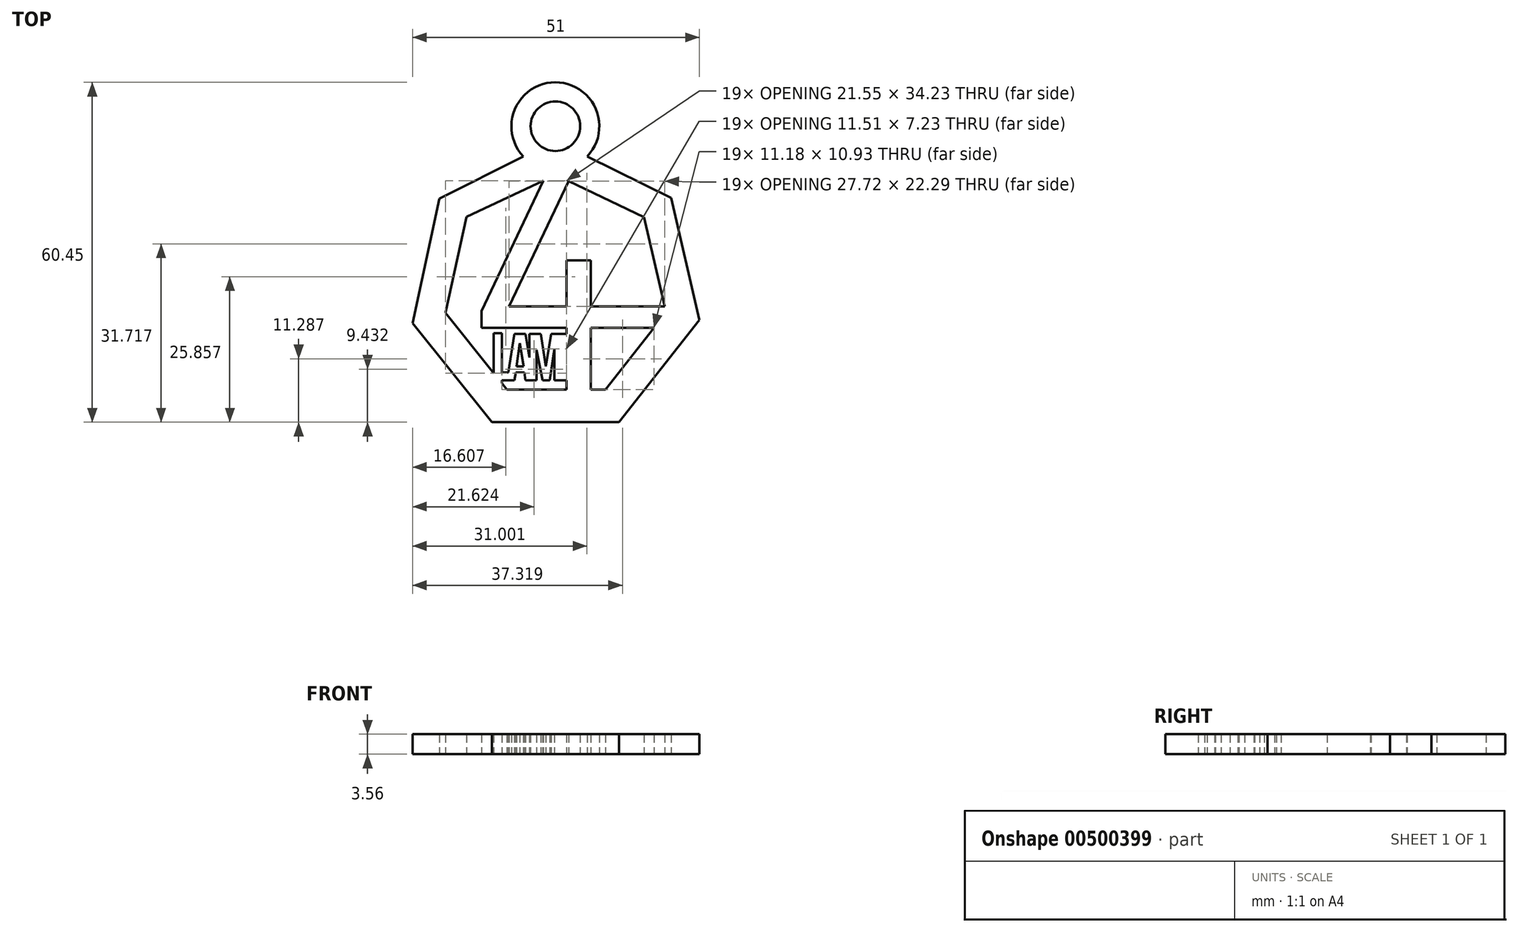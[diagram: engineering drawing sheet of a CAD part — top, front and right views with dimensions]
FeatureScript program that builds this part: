
annotation { "Feature Type Name" : "Feature", "Feature Type Description" : "" }
export const myFeature = defineFeature(function(context is Context, id is Id, definition is map)
    precondition{}
    {
        {
            var Q0;
            Q0=qCreatedBy(makeId("Top.planeOp"),FACE);
            var sketch = newSketch(context, id + "F0", { "sketchPlane" : qUnion([Q0])});
            skPoint(sketch, "E0.middle", {"position": v(0, 0) * mm});
            skLineSegment(sketch, "E1", {"start": v(5.7, 22.4) * mm, "end": v(20.58, 15.04) * mm});
            skLineSegment(sketch, "E2", {"start": v(20.58, 15.04) * mm, "end": v(25.61, -6.7) * mm});
            skLineSegment(sketch, "E3", {"start": v(25.61, -6.7) * mm, "end": v(11.33, -24.87) * mm});
            skLineSegment(sketch, "E4", {"start": v(11.33, -24.87) * mm, "end": v(-11.3, -24.87) * mm});
            skLineSegment(sketch, "E5", {"start": v(-11.3, -24.87) * mm, "end": v(-25.4, -7.27) * mm});
            skLineSegment(sketch, "E6", {"start": v(-25.4, -7.27) * mm, "end": v(-20.6, 14.93) * mm});
            skLineSegment(sketch, "E7", {"start": v(-20.6, 14.93) * mm, "end": v(-5.68, 22.4) * mm});
            skLineSegment(sketch, "E8", {"start": v(-15.79, 11.68) * mm, "end": v(-2.17, 18.1) * mm});
            skLineSegment(sketch, "E9", {"start": v(2.37, 18) * mm, "end": v(15.8, 11.6) * mm});
            skLineSegment(sketch, "E10", {"start": v(15.8, 11.6) * mm, "end": v(19.47, -4.3) * mm});
            skLineSegment(sketch, "E11", {"start": v(17.52, -8.12) * mm, "end": v(8.92, -19.05) * mm});
            skLineSegment(sketch, "E12", {"start": v(8.92, -19.05) * mm, "end": v(6.34, -19.05) * mm});
            skLineSegment(sketch, "E13", {"start": v(-8.61, -19.05) * mm, "end": v(-9.52, -17.92) * mm});
            skLineSegment(sketch, "E14", {"start": v(-19.56, -5.45) * mm, "end": v(-15.79, 11.68) * mm});
            skLineSegment(sketch, "E15", {"start": v(2.37, 18) * mm, "end": v(-8.25, -4.3) * mm});
            skLineSegment(sketch, "E16", {"start": v(-8.25, -4.3) * mm, "end": v(1.99, -4.3) * mm});
            skLineSegment(sketch, "E17", {"start": v(1.99, -4.3) * mm, "end": v(1.99, 3.9) * mm});
            skLineSegment(sketch, "E18", {"start": v(1.99, 3.9) * mm, "end": v(6.34, 3.9) * mm});
            skLineSegment(sketch, "E19", {"start": v(6.34, 3.9) * mm, "end": v(6.34, -4.3) * mm});
            skLineSegment(sketch, "E20", {"start": v(6.34, -4.3) * mm, "end": v(19.47, -4.3) * mm});
            skLineSegment(sketch, "E21", {"start": v(17.52, -8.12) * mm, "end": v(6.34, -8.12) * mm});
            skLineSegment(sketch, "E22", {"start": v(6.34, -8.12) * mm, "end": v(6.34, -19.05) * mm});
            skLineSegment(sketch, "E23", {"start": v(1.99, -19.05) * mm, "end": v(1.99, -17.43) * mm});
            skLineSegment(sketch, "E24", {"start": v(1.99, -8.12) * mm, "end": v(-13.1, -8.12) * mm});
            skLineSegment(sketch, "E25", {"start": v(-13.1, -8.12) * mm, "end": v(-13.1, -5.12) * mm});
            skLineSegment(sketch, "E26", {"start": v(-13.1, -5.12) * mm, "end": v(-2.17, 18.1) * mm});
            skLineSegment(sketch, "E27", {"start": v(-10.97, -16.13) * mm, "end": v(-10.97, -9.02) * mm});
            skLineSegment(sketch, "E28", {"start": v(-10.97, -9.02) * mm, "end": v(-9.52, -9.02) * mm});
            skLineSegment(sketch, "E29", {"start": v(-9.52, -9.02) * mm, "end": v(-9.52, -16) * mm});
            skLineSegment(sketch, "E30", {"start": v(-7.28, -9.15) * mm, "end": v(-5.28, -9.15) * mm});
            skLineSegment(sketch, "E31", {"start": v(-5.28, -9.15) * mm, "end": v(-4.6, -13.39) * mm});
            skLineSegment(sketch, "E32", {"start": v(-4.6, -13.39) * mm, "end": v(-4.6, -9.15) * mm});
            skLineSegment(sketch, "E33", {"start": v(-4.6, -9.15) * mm, "end": v(-2.6, -9.15) * mm});
            skLineSegment(sketch, "E34", {"start": v(-2.6, -9.15) * mm, "end": v(-1.67, -14.94) * mm});
            skLineSegment(sketch, "E35", {"start": v(-1.67, -14.94) * mm, "end": v(-0.73, -9.15) * mm});
            skLineSegment(sketch, "E36", {"start": v(-0.73, -9.15) * mm, "end": v(1.99, -9.15) * mm});
            skLineSegment(sketch, "E37", {"start": v(-7.28, -9.15) * mm, "end": v(-8.38, -16) * mm});
            skLineSegment(sketch, "E38", {"start": v(-8.61, -17.43) * mm, "end": v(-7.28, -17.43) * mm});
            skLineSegment(sketch, "E39", {"start": v(-7.28, -17.43) * mm, "end": v(-7.05, -16) * mm});
            skLineSegment(sketch, "E40", {"start": v(-7.05, -16) * mm, "end": v(-5.53, -16) * mm});
            skLineSegment(sketch, "E41", {"start": v(-5.53, -16) * mm, "end": v(-5.3, -17.43) * mm});
            skLineSegment(sketch, "E42", {"start": v(-5.3, -17.43) * mm, "end": v(-3.35, -17.43) * mm});
            skLineSegment(sketch, "E43", {"start": v(-3.35, -17.43) * mm, "end": v(-3.35, -12.02) * mm});
            skLineSegment(sketch, "E44", {"start": v(-3.35, -12.02) * mm, "end": v(-2.27, -17.43) * mm});
            skLineSegment(sketch, "E45", {"start": v(-2.27, -17.43) * mm, "end": v(-1, -17.43) * mm});
            skLineSegment(sketch, "E46", {"start": v(-1, -17.43) * mm, "end": v(-0.2, -11.82) * mm});
            skLineSegment(sketch, "E47", {"start": v(-0.2, -11.82) * mm, "end": v(-0.2, -17.43) * mm});
            skLineSegment(sketch, "E48", {"start": v(-0.2, -17.43) * mm, "end": v(1.99, -17.43) * mm});
            skLineSegment(sketch, "E49", {"start": v(-6.32, -10.81) * mm, "end": v(-6.9, -14.94) * mm});
            skLineSegment(sketch, "E50", {"start": v(-6.9, -14.94) * mm, "end": v(-5.6, -14.94) * mm});
            skLineSegment(sketch, "E51", {"start": v(-5.6, -14.94) * mm, "end": v(-6.32, -10.81) * mm});
            skLineSegment(sketch, "E52.trimOffspring", {"start": v(1.99, -9.15) * mm, "end": v(1.99, -8.12) * mm});
            skLineSegment(sketch, "E53.trimOffspring", {"start": v(-10.97, -16.13) * mm, "end": v(-19.56, -5.45) * mm});
            skPoint(sketch, "E54.orphan", {"position": v(0, 19.12) * mm});
            skLineSegment(sketch, "E55", {"start": v(-8.61, -17.43) * mm, "end": v(-9.52, -17.43) * mm});
            skLineSegment(sketch, "E56", {"start": v(-8.38, -16) * mm, "end": v(-9.52, -16) * mm});
            skLineSegment(sketch, "E57.trimOffspring", {"start": v(-9.52, -17.43) * mm, "end": v(-9.52, -17.92) * mm});
            skLineSegment(sketch, "E58.trimOffspring", {"start": v(1.99, -19.05) * mm, "end": v(-8.61, -19.05) * mm});
            skArc(sketch, "E59", {"start": v(5.7, 22.4) * mm, "mid": v(-0.01, 35.58) * mm, "end": v(-5.68, 22.4) * mm});
            skCircle(sketch, "E60", {"center": v(0, 27.77) * mm, "radius": 4.4 * mm});
            skPoint(sketch, "E61.orphan", {"position": v(0, 25.23) * mm});
            skSolve(sketch);
        }
        {
            var Q0;
            Q0 = qSketchRegion(id + "F0", true);
            extrude(context, id + "F1", {"entities" : qUnion([Q0]), "depth" : 3.56 * mm});
        }
    });
